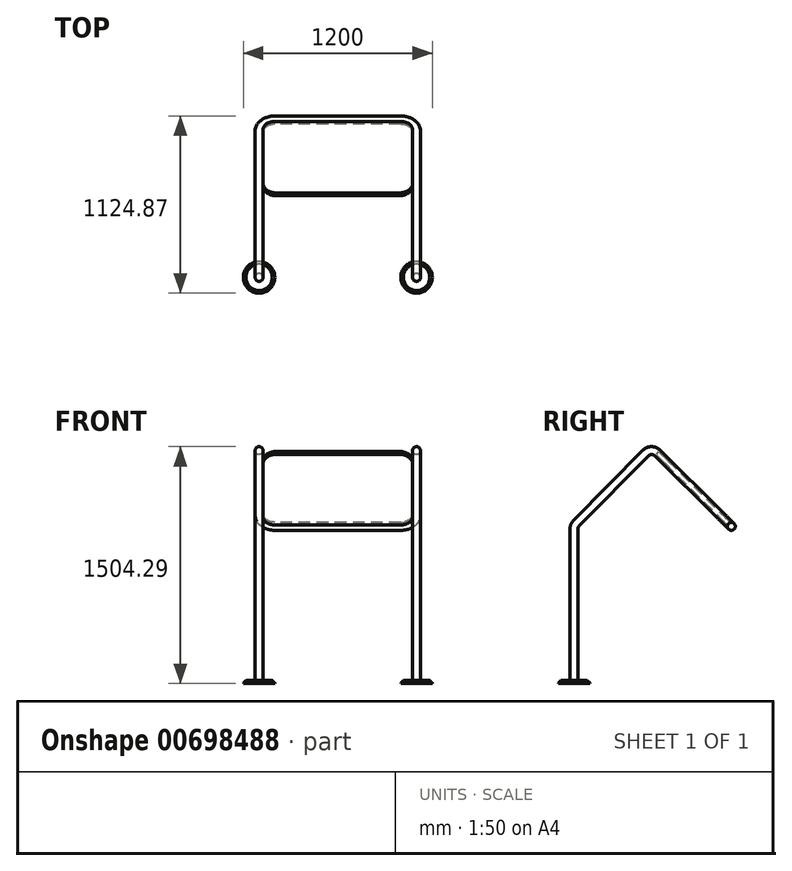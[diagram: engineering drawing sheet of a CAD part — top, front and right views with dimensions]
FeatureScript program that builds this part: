
annotation { "Feature Type Name" : "Feature", "Feature Type Description" : "" }
export const myFeature = defineFeature(function(context is Context, id is Id, definition is map)
    precondition{}
    {
        {
            var Q0;
            Q0=qCreatedBy(makeId("Right.planeOp"),FACE);
            var sketch = newSketch(context, id + "F0", { "sketchPlane" : qUnion([Q0])});
            skLineSegment(sketch, "E0", {"start": v(-999.87, 0) * mm, "end": v(-999.87, 981.85) * mm});
            skLineSegment(sketch, "E1", {"start": v(-985.41, 1017.02) * mm, "end": v(-542.63, 1464.46) * mm});
            skLineSegment(sketch, "E2", {"start": v(-471.93, 1464.83) * mm, "end": v(0, 997.82) * mm});
            skPoint(sketch, "E3.visualSharp", {"position": v(-999.87, 1002.4) * mm});
            skArc(sketch, "E3.filletArc", {"start": v(-985.41, 1017.02) * mm, "mid": v(-996.12, 1000.87) * mm, "end": v(-999.87, 981.85) * mm});
            skPoint(sketch, "E4.visualSharp", {"position": v(-507.47, 1500) * mm});
            skArc(sketch, "E4.filletArc", {"start": v(-471.93, 1464.83) * mm, "mid": v(-507.36, 1479.29) * mm, "end": v(-542.63, 1464.46) * mm});
            skSolve(sketch);
        }
        {
            var Q0;
            Q0=sQuery(id+"F0.wireOp",EDGE,"E4.filletArc");
            var Q1;
            Q1=sQuery(id+"F0.wireOp",EDGE,"E2");
            var Q2;
            Q2=sQuery(id+"F0.wireOp",EDGE,"E1");
            var Q3;
            Q3=sQuery(id+"F0.wireOp",EDGE,"E0");
            var Q4;
            Q4=sQuery(id+"F0.wireOp",EDGE,"E3.filletArc");
            extrude(context, id + "F1", {"bodyType" : ToolBodyType.SURFACE, "surfaceEntities" : qUnion([Q0, Q1, Q2, Q3, Q4]), "endBound" : BoundingType.SYMMETRIC, "depth" : 1000 * mm, "offsetDistance" : 25 * mm});
        }
        {
            var Q0;
            Q0=makeQuery(id+"F1.opExtrude","SWEPT_FACE",FACE,{"disambiguationData":[OSD([sQuery(id+"F0.wireOp",EDGE,"E2")])]});
            var sketch = newSketch(context, id + "F2", { "sketchPlane" : qUnion([Q0])});
            skLineSegment(sketch, "E5.0.0", {"start": v(500, -801.86) * mm, "end": v(500, -1365.8) * mm});
            skLineSegment(sketch, "E5.0.1", {"start": v(400, -701.86) * mm, "end": v(-400, -701.86) * mm});
            skLineSegment(sketch, "E5.0.2", {"start": v(-500, -801.86) * mm, "end": v(-500, -1365.8) * mm});
            skLineSegment(sketch, "E5.0.3", {"start": v(-500, -1365.8) * mm, "end": v(500, -1365.8) * mm});
            skPoint(sketch, "E6.visualSharp", {"position": v(500, -701.86) * mm});
            skArc(sketch, "E6.filletArc", {"start": v(500, -801.86) * mm, "mid": v(470.71, -731.15) * mm, "end": v(400, -701.86) * mm});
            skPoint(sketch, "E7.visualSharp", {"position": v(-500, -701.86) * mm});
            skArc(sketch, "E7.filletArc", {"start": v(-400, -701.86) * mm, "mid": v(-470.71, -731.15) * mm, "end": v(-500, -801.86) * mm});
            skSolve(sketch);
        }
        {
            var Q0;
            Q0=qCreatedBy(makeId("Top.planeOp"),FACE);
            var sketch = newSketch(context, id + "F3", { "sketchPlane" : qUnion([Q0])});
            skPoint(sketch, "E8.0", {"position": v(500, -999.87) * mm});
            skCircle(sketch, "E9", {"center": v(500, -999.87) * mm, "radius": 25 * mm});
            skSolve(sketch);
        }
        {
            var Q0;
            Q0=makeQuery(id+"F3.imprint","IMPRINT",FACE,{"disambiguationData":[TD([[makeQuery(id+"F3.imprint","IMPRINT",EDGE,{"derivedFrom":sQuery(id+"F3.wireOp",EDGE,"E9")}),1.0]])]});
            var Q1;
            Q1=makeQuery(id+"F1.opExtrude","CAP_EDGE",EDGE,{"disambiguationData":[OSD([sQuery(id+"F0.wireOp",EDGE,"E0")])],"isStart":false});
            var Q2;
            Q2=makeQuery(id+"F1.opExtrude","CAP_EDGE",EDGE,{"disambiguationData":[OSD([sQuery(id+"F0.wireOp",EDGE,"E1")])],"isStart":false});
            var Q3;
            Q3=makeQuery(id+"F1.opExtrude","CAP_EDGE",EDGE,{"disambiguationData":[OSD([sQuery(id+"F0.wireOp",EDGE,"E3.filletArc")])],"isStart":false});
            var Q4;
            Q4=makeQuery(id+"F1.opExtrude","CAP_EDGE",EDGE,{"disambiguationData":[OSD([sQuery(id+"F0.wireOp",EDGE,"E4.filletArc")])],"isStart":false});
            var Q5;
            Q5=sQuery(id+"F2.wireOp",EDGE,"E5.0.0");
            var Q6;
            Q6=sQuery(id+"F2.wireOp",EDGE,"E6.filletArc");
            var Q7;
            Q7=sQuery(id+"F2.wireOp",EDGE,"E5.0.1");
            var Q8;
            Q8=sQuery(id+"F2.wireOp",EDGE,"E7.filletArc");
            var Q9;
            Q9=sQuery(id+"F2.wireOp",EDGE,"E5.0.2");
            var Q10;
            Q10=makeQuery(id+"F1.opExtrude","CAP_EDGE",EDGE,{"disambiguationData":[OSD([sQuery(id+"F0.wireOp",EDGE,"E4.filletArc")])],"isStart":true});
            var Q11;
            Q11=makeQuery(id+"F1.opExtrude","CAP_EDGE",EDGE,{"disambiguationData":[OSD([sQuery(id+"F0.wireOp",EDGE,"E1")])],"isStart":true});
            var Q12;
            Q12=makeQuery(id+"F1.opExtrude","CAP_EDGE",EDGE,{"disambiguationData":[OSD([sQuery(id+"F0.wireOp",EDGE,"E3.filletArc")])],"isStart":true});
            var Q13;
            Q13=makeQuery(id+"F1.opExtrude","CAP_EDGE",EDGE,{"disambiguationData":[OSD([sQuery(id+"F0.wireOp",EDGE,"E0")])],"isStart":true});
            sweep(context, id + "F4", {"profiles" : qUnion([Q0]), "path" : qUnion([Q1, Q2, Q3, Q4, Q5, Q6, Q7, Q8, Q9, Q10, Q11, Q12, Q13])});
        }
        {
            var Q0;
            Q0=makeQuery(id+"F1.opExtrude","SWEPT_FACE",FACE,{"disambiguationData":[OSD([sQuery(id+"F0.wireOp",EDGE,"E2")])]});
            var sketch = newSketch(context, id + "F5", { "sketchPlane" : qUnion([Q0])});
            skLineSegment(sketch, "E10", {"start": v(525, -801.86) * mm, "end": v(525, -1365.8) * mm});
            skLineSegment(sketch, "E11", {"start": v(475, -1365.8) * mm, "end": v(475, -801.86) * mm});
            skArc(sketch, "E12", {"start": v(525, -801.86) * mm, "mid": v(488.39, -713.47) * mm, "end": v(400, -676.86) * mm});
            skArc(sketch, "E13", {"start": v(475, -801.86) * mm, "mid": v(453.03, -748.83) * mm, "end": v(400, -726.86) * mm});
            skLineSegment(sketch, "E14", {"start": v(-400, -676.86) * mm, "end": v(400, -676.86) * mm});
            skLineSegment(sketch, "E15", {"start": v(400, -726.86) * mm, "end": v(-400, -726.86) * mm});
            skLineSegment(sketch, "E16", {"start": v(-525, -1365.8) * mm, "end": v(-525, -801.86) * mm});
            skLineSegment(sketch, "E17", {"start": v(-475, -801.86) * mm, "end": v(-475, -1365.8) * mm});
            skLineSegment(sketch, "E18", {"start": v(475, -1365.8) * mm, "end": v(-475, -1365.8) * mm});
            skArc(sketch, "E19", {"start": v(-400, -726.86) * mm, "mid": v(-453.03, -748.83) * mm, "end": v(-475, -801.86) * mm});
            skSolve(sketch);
        }
        {
            var Q0;
            Q0=makeQuery(id+"F5.imprint","IMPRINT",FACE,{"disambiguationData":[TD([[makeQuery(id+"F5.imprint","IMPRINT",EDGE,{"derivedFrom":sQuery(id+"F5.wireOp",EDGE,"E11")}),1.0]])]});
            extrude(context, id + "F6", {"entities" : qUnion([Q0]), "operationType" : NewBodyOperationType.ADD, "endBound" : BoundingType.SYMMETRIC, "depth" : 25 * mm, "offsetDistance" : 25 * mm});
        }
        {
            var Q0;
            Q0=makeQuery(id+"F6.opExtrude","SWEPT_EDGE",EDGE,{"disambiguationData":[OSD([sQuery(id+"F0.wireOp",VERTEX,"E2.start"),sQuery(id+"F5.wireOp",EDGE,"E11"),sQuery(id+"F5.wireOp",EDGE,"E18")])]});
            var Q1;
            Q1=makeQuery(id+"F6.opExtrude","SWEPT_EDGE",EDGE,{"disambiguationData":[OSD([sQuery(id+"F0.wireOp",VERTEX,"E2.start"),sQuery(id+"F5.wireOp",EDGE,"E17"),sQuery(id+"F5.wireOp",EDGE,"E18")])]});
            fillet(context, id + "F7", {"entities" : qUnion([Q0, Q1]), "radius" : 85 * mm, "tangentPropagation" : true, "allowEdgeOverflow" : false});
        }
        {
            var Q0;
            Q0=makeQuery(id+"F3.imprint","IMPRINT",FACE,{"disambiguationData":[TD([[makeQuery(id+"F3.imprint","IMPRINT",EDGE,{"derivedFrom":sQuery(id+"F3.wireOp",EDGE,"E9")}),1.0]])]});
            var sketch = newSketch(context, id + "F8", { "sketchPlane" : qUnion([Q0])});
            skCircle(sketch, "E20.0.0", {"center": v(-500, -999.87) * mm, "radius": 25 * mm, "construction": true});
            skCircle(sketch, "E21.0.0", {"center": v(500, -999.87) * mm, "radius": 25 * mm, "construction": true});
            skCircle(sketch, "E22", {"center": v(500, -999.87) * mm, "radius": 100 * mm});
            skCircle(sketch, "E23", {"center": v(-500, -999.87) * mm, "radius": 100 * mm});
            skSolve(sketch);
        }
        {
            var Q0;
            Q0=makeQuery(id+"F8.imprint","IMPRINT",FACE,{"disambiguationData":[TD([[makeQuery(id+"F8.imprint","IMPRINT",EDGE,{"derivedFrom":sQuery(id+"F8.wireOp",EDGE,"E22")}),1.0]])]});
            var Q1;
            Q1=makeQuery(id+"F8.imprint","IMPRINT",FACE,{"disambiguationData":[TD([[makeQuery(id+"F8.imprint","IMPRINT",EDGE,{"derivedFrom":sQuery(id+"F8.wireOp",EDGE,"E23")}),1.0]])]});
            extrude(context, id + "F9", {"entities" : qUnion([Q0, Q1]), "operationType" : NewBodyOperationType.ADD, "depth" : 20 * mm, "offsetDistance" : 25 * mm});
        }
        {
            var Q0;
            Q0=makeQuery(id+"F9.opExtrude","CAP_EDGE",EDGE,{"disambiguationData":[OSD([sQuery(id+"F8.wireOp",EDGE,"E22")])],"isStart":false});
            var Q1;
            Q1=makeQuery(id+"F9.opExtrude","CAP_EDGE",EDGE,{"disambiguationData":[OSD([sQuery(id+"F8.wireOp",EDGE,"E23")])],"isStart":false});
            chamfer(context, id + "F10", {"entities" : qUnion([Q0, Q1]), "width" : 16 * mm, "tangentPropagation" : true});
        }
    });
